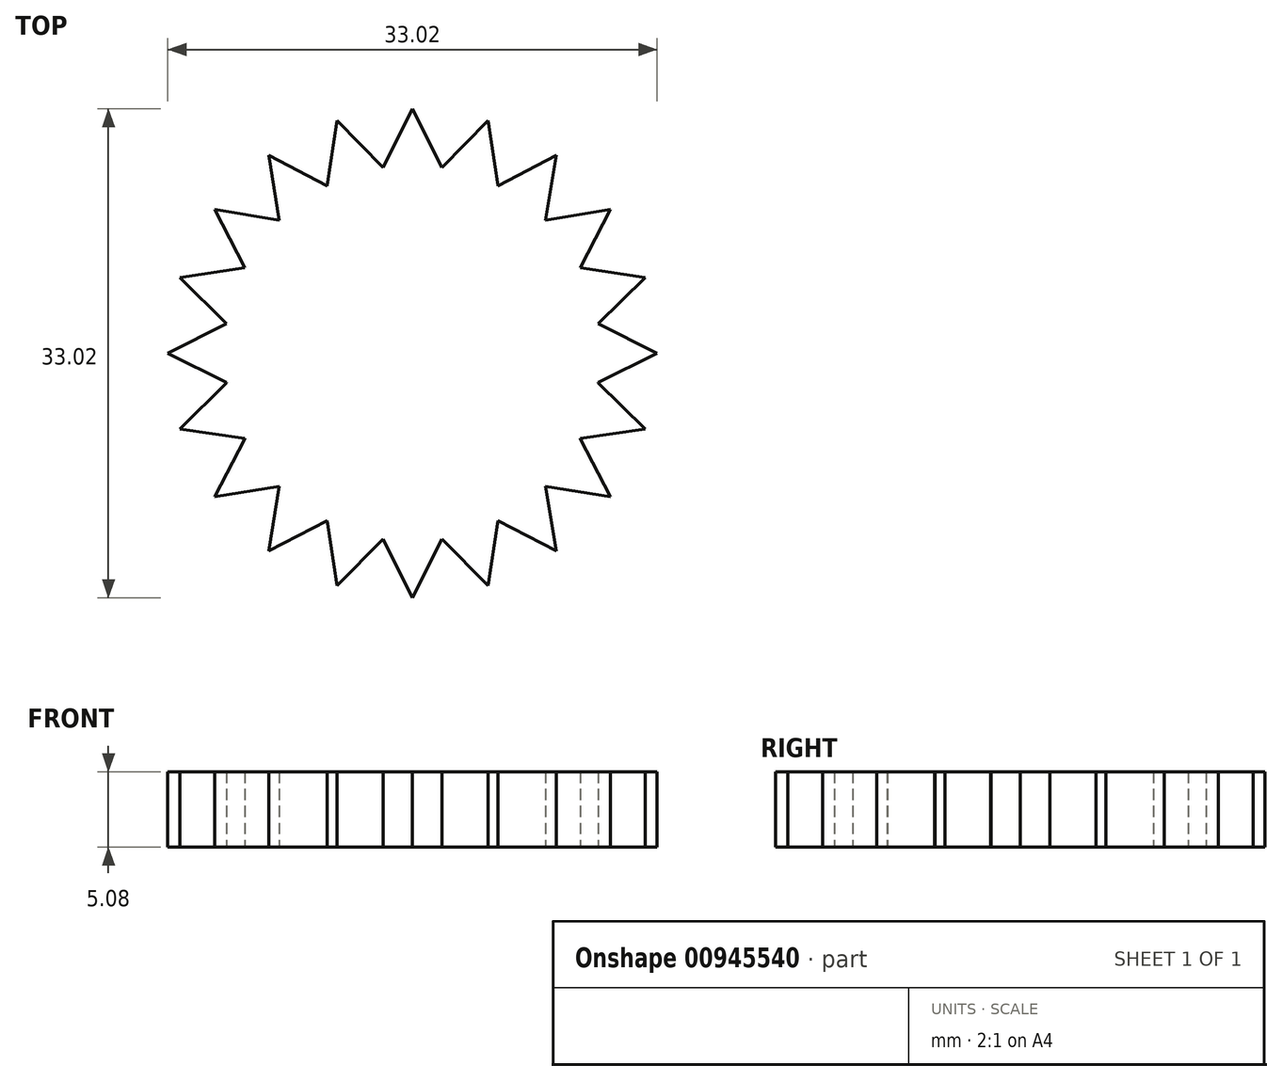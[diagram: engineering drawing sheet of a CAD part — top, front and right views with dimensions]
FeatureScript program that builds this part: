
annotation { "Feature Type Name" : "Feature", "Feature Type Description" : "" }
export const myFeature = defineFeature(function(context is Context, id is Id, definition is map)
    precondition{}
    {
        {
            var Q0;
            Q0=qCreatedBy(makeId("Top.planeOp"),FACE);
            var sketch = newSketch(context, id + "F0", { "sketchPlane" : qUnion([Q0])});
            skCircle(sketch, "E0", {"center": v(0, 0) * mm, "radius": 12.7 * mm});
            skCircle(sketch, "E1", {"center": v(0, 0) * mm, "radius": 11.43 * mm});
            skCircle(sketch, "E2", {"center": v(0, 0) * mm, "radius": 3.81 * mm});
            skCircle(sketch, "E3", {"center": v(0, 0) * mm, "radius": 5.08 * mm});
            skLineSegment(sketch, "E4", {"start": v(-12.54, 1.98) * mm, "end": v(-12.54, -1.98) * mm});
            skLineSegment(sketch, "E5", {"start": v(-12.54, 0) * mm, "end": v(-16.5, 0) * mm});
            skLineSegment(sketch, "E6", {"start": v(-12.54, -1.98) * mm, "end": v(-16.5, 0) * mm});
            skLineSegment(sketch, "E7", {"start": v(-12.54, 1.98) * mm, "end": v(-16.5, 0) * mm});
            skLineSegment(sketch, "E8.1.0", {"start": v(-11.32, -5.76) * mm, "end": v(-15.7, -5.1) * mm});
            skLineSegment(sketch, "E8.1.1", {"start": v(-12.54, -2) * mm, "end": v(-15.7, -5.1) * mm});
            skLineSegment(sketch, "E8.2.0", {"start": v(-8.98, -8.98) * mm, "end": v(-13.35, -9.7) * mm});
            skLineSegment(sketch, "E8.2.1", {"start": v(-11.31, -5.77) * mm, "end": v(-13.35, -9.7) * mm});
            skLineSegment(sketch, "E8.3.0", {"start": v(-5.77, -11.31) * mm, "end": v(-9.7, -13.35) * mm});
            skLineSegment(sketch, "E8.3.1", {"start": v(-8.98, -8.98) * mm, "end": v(-9.7, -13.35) * mm});
            skLineSegment(sketch, "E8.4.0", {"start": v(-2, -12.54) * mm, "end": v(-5.1, -15.7) * mm});
            skLineSegment(sketch, "E8.4.1", {"start": v(-5.76, -11.32) * mm, "end": v(-5.1, -15.7) * mm});
            skLineSegment(sketch, "E8.5.0", {"start": v(1.98, -12.54) * mm, "end": v(0, -16.5) * mm});
            skLineSegment(sketch, "E8.5.1", {"start": v(-1.98, -12.54) * mm, "end": v(0, -16.5) * mm});
            skLineSegment(sketch, "E8.6.0", {"start": v(5.76, -11.32) * mm, "end": v(5.1, -15.7) * mm});
            skLineSegment(sketch, "E8.6.1", {"start": v(2, -12.54) * mm, "end": v(5.1, -15.7) * mm});
            skLineSegment(sketch, "E8.7.0", {"start": v(8.98, -8.98) * mm, "end": v(9.7, -13.35) * mm});
            skLineSegment(sketch, "E8.7.1", {"start": v(5.77, -11.31) * mm, "end": v(9.7, -13.35) * mm});
            skLineSegment(sketch, "E8.8.0", {"start": v(11.31, -5.77) * mm, "end": v(13.35, -9.7) * mm});
            skLineSegment(sketch, "E8.8.1", {"start": v(8.98, -8.98) * mm, "end": v(13.35, -9.7) * mm});
            skLineSegment(sketch, "E8.9.0", {"start": v(12.54, -2) * mm, "end": v(15.7, -5.1) * mm});
            skLineSegment(sketch, "E8.9.1", {"start": v(11.32, -5.76) * mm, "end": v(15.7, -5.1) * mm});
            skLineSegment(sketch, "E8.10.0", {"start": v(12.54, 1.98) * mm, "end": v(16.5, 0) * mm});
            skLineSegment(sketch, "E8.10.1", {"start": v(12.54, -1.98) * mm, "end": v(16.5, 0) * mm});
            skLineSegment(sketch, "E8.11.0", {"start": v(11.32, 5.76) * mm, "end": v(15.7, 5.1) * mm});
            skLineSegment(sketch, "E8.11.1", {"start": v(12.54, 2) * mm, "end": v(15.7, 5.1) * mm});
            skLineSegment(sketch, "E8.12.0", {"start": v(8.98, 8.98) * mm, "end": v(13.35, 9.7) * mm});
            skLineSegment(sketch, "E8.12.1", {"start": v(11.31, 5.77) * mm, "end": v(13.35, 9.7) * mm});
            skLineSegment(sketch, "E8.13.0", {"start": v(5.77, 11.31) * mm, "end": v(9.7, 13.35) * mm});
            skLineSegment(sketch, "E8.13.1", {"start": v(8.98, 8.98) * mm, "end": v(9.7, 13.35) * mm});
            skLineSegment(sketch, "E8.14.0", {"start": v(2, 12.54) * mm, "end": v(5.1, 15.7) * mm});
            skLineSegment(sketch, "E8.14.1", {"start": v(5.76, 11.32) * mm, "end": v(5.1, 15.7) * mm});
            skLineSegment(sketch, "E8.15.0", {"start": v(-1.98, 12.54) * mm, "end": v(0, 16.5) * mm});
            skLineSegment(sketch, "E8.15.1", {"start": v(1.98, 12.54) * mm, "end": v(0, 16.5) * mm});
            skLineSegment(sketch, "E8.16.0", {"start": v(-5.76, 11.32) * mm, "end": v(-5.1, 15.7) * mm});
            skLineSegment(sketch, "E8.16.1", {"start": v(-2, 12.54) * mm, "end": v(-5.1, 15.7) * mm});
            skLineSegment(sketch, "E8.17.0", {"start": v(-8.98, 8.98) * mm, "end": v(-9.7, 13.35) * mm});
            skLineSegment(sketch, "E8.17.1", {"start": v(-5.77, 11.31) * mm, "end": v(-9.7, 13.35) * mm});
            skLineSegment(sketch, "E8.18.0", {"start": v(-11.31, 5.77) * mm, "end": v(-13.35, 9.7) * mm});
            skLineSegment(sketch, "E8.18.1", {"start": v(-8.98, 8.98) * mm, "end": v(-13.35, 9.7) * mm});
            skLineSegment(sketch, "E8.19.0", {"start": v(-12.54, 2) * mm, "end": v(-15.7, 5.1) * mm});
            skLineSegment(sketch, "E8.19.1", {"start": v(-11.32, 5.76) * mm, "end": v(-15.7, 5.1) * mm});
            skSolve(sketch);
        }
        {
            var Q0;
            Q0 = qSketchRegion(id + "F0", true);
            var Q1;
            Q1=makeQuery(id+"F0.imprint","IMPRINT",FACE,{"disambiguationData":[TD([[makeQuery(id+"F0.imprint","IMPRINT",EDGE,{"derivedFrom":sQuery(id+"F0.wireOp",EDGE,"E1")}),1.0]])]});
            var Q2;
            Q2=makeQuery(id+"F0.imprint","IMPRINT",FACE,{"disambiguationData":[TD([[makeQuery(id+"F0.imprint","IMPRINT",EDGE,{"derivedFrom":sQuery(id+"F0.wireOp",EDGE,"E2")}),1.0]])]});
            var Q3;
            Q3=makeQuery(id+"F0.imprint","IMPRINT",FACE,{"disambiguationData":[TD([[makeQuery(id+"F0.imprint","IMPRINT",EDGE,{"derivedFrom":sQuery(id+"F0.wireOp",EDGE,"E2")}),-1.0]])]});
            extrude(context, id + "F1", {"entities" : qUnion([Q0, Q1, Q2, Q3]), "depth" : 5.08 * mm, "offsetDistance" : 25.4 * mm});
        }
    });
